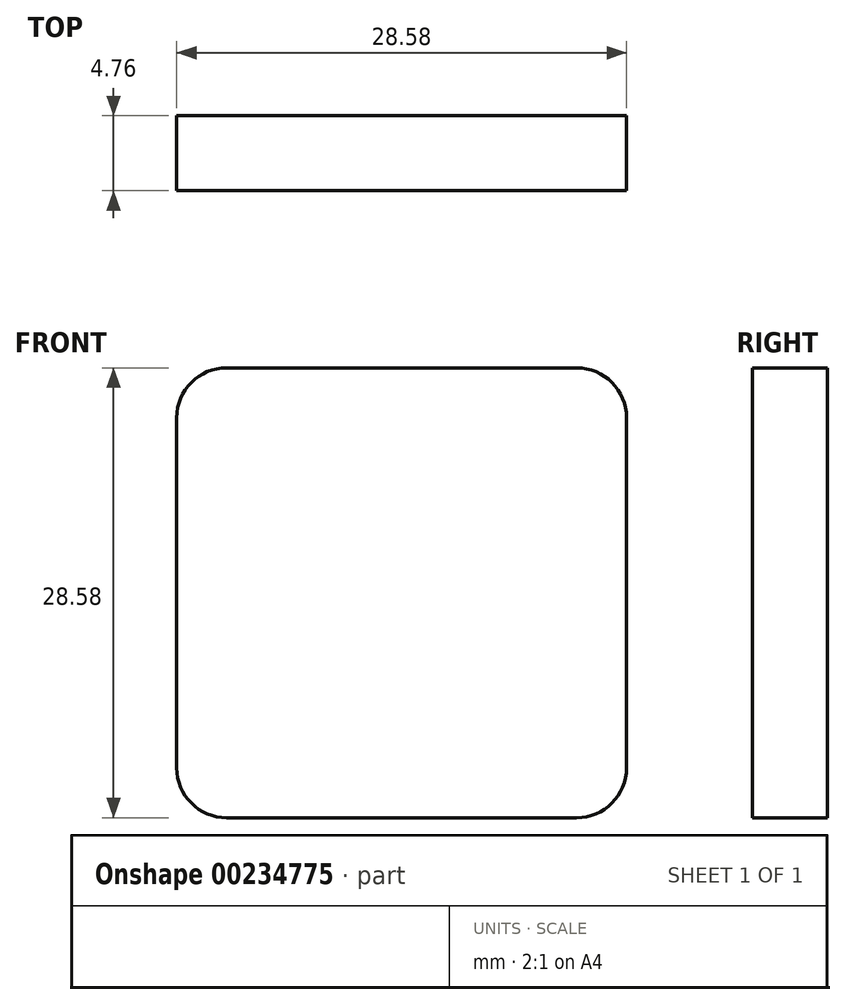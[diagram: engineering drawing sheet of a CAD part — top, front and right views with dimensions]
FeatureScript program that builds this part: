
annotation { "Feature Type Name" : "Feature", "Feature Type Description" : "" }
export const myFeature = defineFeature(function(context is Context, id is Id, definition is map)
    precondition{}
    {
        {
            var Q0;
            Q0=qCreatedBy(makeId("Front.planeOp"),FACE);
            var sketch = newSketch(context, id + "F0", { "sketchPlane" : qUnion([Q0])});
            skLineSegment(sketch, "E0.bottom", {"start": v(15.88, -19.05) * mm, "end": v(-15.88, -19.05) * mm});
            skLineSegment(sketch, "E0.top", {"start": v(15.88, 19.05) * mm, "end": v(-15.88, 19.05) * mm});
            skLineSegment(sketch, "E0.left", {"start": v(19.05, -15.88) * mm, "end": v(19.05, 15.88) * mm});
            skLineSegment(sketch, "E0.right", {"start": v(-19.05, -15.88) * mm, "end": v(-19.05, 15.87) * mm});
            skPoint(sketch, "E0.middle", {"position": v(0, 0) * mm});
            skLineSegment(sketch, "E1.bottom", {"start": v(11.11, -14.29) * mm, "end": v(-11.11, -14.29) * mm});
            skLineSegment(sketch, "E1.top", {"start": v(11.11, 14.29) * mm, "end": v(-11.11, 14.29) * mm});
            skLineSegment(sketch, "E1.left", {"start": v(14.29, -11.11) * mm, "end": v(14.29, 11.11) * mm});
            skLineSegment(sketch, "E1.right", {"start": v(-14.29, -11.11) * mm, "end": v(-14.29, 11.11) * mm});
            skPoint(sketch, "E2.visualSharp", {"position": v(-19.05, 19.05) * mm});
            skArc(sketch, "E2.filletArc", {"start": v(-15.88, 19.05) * mm, "mid": v(-18.12, 18.12) * mm, "end": v(-19.05, 15.87) * mm});
            skPoint(sketch, "E3.visualSharp", {"position": v(19.05, 19.05) * mm});
            skArc(sketch, "E3.filletArc", {"start": v(19.05, 15.88) * mm, "mid": v(18.12, 18.12) * mm, "end": v(15.88, 19.05) * mm});
            skPoint(sketch, "E4.visualSharp", {"position": v(14.29, 14.29) * mm});
            skArc(sketch, "E4.filletArc", {"start": v(14.29, 11.11) * mm, "mid": v(13.36, 13.36) * mm, "end": v(11.11, 14.29) * mm});
            skPoint(sketch, "E5.visualSharp", {"position": v(-14.29, 14.29) * mm});
            skArc(sketch, "E5.filletArc", {"start": v(-11.11, 14.29) * mm, "mid": v(-13.36, 13.36) * mm, "end": v(-14.29, 11.11) * mm});
            skPoint(sketch, "E6.visualSharp", {"position": v(-14.29, -14.29) * mm});
            skArc(sketch, "E6.filletArc", {"start": v(-14.29, -11.11) * mm, "mid": v(-13.36, -13.36) * mm, "end": v(-11.11, -14.29) * mm});
            skPoint(sketch, "E7.visualSharp", {"position": v(-19.05, -19.05) * mm});
            skArc(sketch, "E7.filletArc", {"start": v(-19.05, -15.88) * mm, "mid": v(-18.12, -18.12) * mm, "end": v(-15.88, -19.05) * mm});
            skPoint(sketch, "E8.visualSharp", {"position": v(14.29, -14.29) * mm});
            skArc(sketch, "E8.filletArc", {"start": v(11.11, -14.29) * mm, "mid": v(13.36, -13.36) * mm, "end": v(14.29, -11.11) * mm});
            skPoint(sketch, "E9.visualSharp", {"position": v(19.05, -19.05) * mm});
            skArc(sketch, "E9.filletArc", {"start": v(15.88, -19.05) * mm, "mid": v(18.12, -18.12) * mm, "end": v(19.05, -15.88) * mm});
            skSolve(sketch);
        }
        {
            var Q0;
            Q0=makeQuery(id+"F0.imprint","IMPRINT",FACE,{"disambiguationData":[TD([[makeQuery(id+"F0.imprint","IMPRINT",EDGE,{"derivedFrom":sQuery(id+"F0.wireOp",EDGE,"E1.bottom")}),-1.0]])]});
            extrude(context, id + "F1", {"entities" : qUnion([Q0]), "depth" : 4.76 * mm});
        }
    });
